# Revit family: PRD_FrankeWS_SpDspnsrs_EXOSSoapDispenser_EXOS618EX_618EB_618EW
name_source: partatom
category: Specialty Equipment
revit_build: Autodesk Revit 2018 (Build: 20190510_1515(x64)
units: mm (PartAtom-declared; Revit-internal decimal feet)

## family parameters
Cut with Voids When Loaded = No
Host = Face
OmniClass Number = 23.40.20.21.34
OmniClass Title = Soap Holders, Dispensers
Part Type = Normal
Room Calculation Point = No
Round Connector Dimension = Use Diameter
Shared = No

## types (3) — shared parameters
AssetType = Fixed
Category = Pr_40_70_22_81, Soap dispensers
Default Elevation = 1200 mm
DispenserMaterial = PRD_AR_StainlessSteel_SatinFinished
DurationUnit = year
Features = stainless steel, satin finished
FillingQuantity = 0.8
FillingQuantityUom = Liter
Finish = Satin finished
IfcExportAs = IfcFurnitureType
IfcExportType = USERDEFINED
IntegralAccessories = incl. mounting materials
IsBuiltIn = TRUE
Lock = Key-lock
MainColor = Stainless steel
Manufacturer = KWC Group AG
ManufacturerName = KWC Group AG
ManufacturerURL = www.kwc.com
Material = Stainless steel
MaterialCode = 1.4301
MaterialThickness = 1.20 mm
NBSDescription = Soap dispensers
NBSReference = 45-35-72/358
NominalDepth = 120 mm  [stored 0.393701 ft]
NominalHeight = 500 mm  [stored 1.64042 ft]
NominalWidth = 124 mm  [stored 0.406824 ft]
ProductInformation = https://pim.kwc.com
Size = 124 x 500 x 120 mm
Style = Dispenser
SurfaceTreatment = InoxPlus (anti fingerprint)
TypeOfConsumable = Foam soap
TypeOfFixing = Screw
TypeOfMounting = Recessed mounting
TypeOfOperation = Manual operation
TypeOfSoapContainer = Integrated refillable tank
URL = www.kwc.com
Uniclass2015Code = Pr_40_70_22_81
Uniclass2015Title = Soap dispenser
Uniclass2015Version = Products v1.17
Version = 1
WarrantyDurationUnit = year

## per-type parameters (varying)
| type | BIMObjectName | Description | GrossWeight | ModelNumber | Name | NetWeight | PanelMaterial |
| EXOS618EX | PRD_AR_SoapDispensers_EXOSSoapDispenser_EXOS618EX | Soap dispenser for recessed mounting, stainless steel with satin finish, front and casing with InoxPlus surface refinement for the reduction of finger marks and better cleaning characteristics (easy to clean), material thickness 1.2 mm, suitable for liquid soap and lotions, 800 ml refill tank, with stainless steel push lever, easy to refill with soap tank on front panel, includes mounting materials. | 3.58 kg | 2030034637 | Soap dispenser EXOS618EX | 2.58 kg | PRD_AR_StainlessSteel_SatinFinished |
| EXOS618EB | PRD_AR_SoapDispensers_EXOSSoapDispenser_EXOS618EB | Soap dispenser for recessed mounting, stainless steel with satin finish, black safety glass front panel, casing with InoxPlus surface refinement for the reduction of finger marks and better cleaning characteristics (easy to clean), material thickness 1.2 mm, suitable for liquid soap and lotions, 800 ml refill tank, with stainless steel push lever, easy to refill with soap tank on front panel, includes mounting materials. | 3.80 kg | 2030034638 | Soap dispenser EXOS618EB | 2.80 kg | PRD_AR_Glass_Black |
| EXOS618EW | PRD_AR_SoapDispensers_EXOSSoapDispenser_EXOS618EW | Soap dispenser for recessed mounting, stainless steel with satin finish, white safety glass front panel, casing with InoxPlus surface refinement for the reduction of finger marks and better cleaning characteristics (easy to clean), material thickness 1.2 mm, suitable for liquid soap and lotions, 800 ml refill tank, with stainless steel push lever, easy to refill with soap tank on front panel, includes mounting materials. | 3.80 kg | 2030034667 | Soap dispenser EXOS618EW | 2.80 kg | PRD_AR_Glass_White |

note: column(s) folded — value = type name in every type: Model, ModelReference

note: [stored X ft] marks values corroborated as IEEE doubles in the binary element streams (Revit-internal decimal feet)

## geometry (parser evidence)
native form markers: Sweep x5
no freeform markers — native parametric forms only
